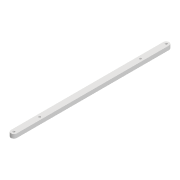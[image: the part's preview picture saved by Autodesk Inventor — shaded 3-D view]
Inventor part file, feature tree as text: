
AUTODESK INVENTOR PART (.ipt)
format: ipt  version: 2022 (Build 260153000, 153)  size: 94,720 bytes
history: native  units: mm
features: extrude x1, sketch x1
ambient origin geometry x8: Origin, YZ Plane, XZ Plane, XY Plane, X Axis, Y Axis, Z Axis, Center Point
bodies: Solid1 (feature_tree)
feature tree (2):
  extrude  "Extrusion1"  Depth=127.773mm
  sketch  "Sketch1"  dims[d0=2.2mm d1=2.2mm d2=6.0mm d3=153.89mm d6=4.0mm d7=0.0mm d10=2.2mm d11=25.907mm d12=2.2mm d13=127.773mm]
